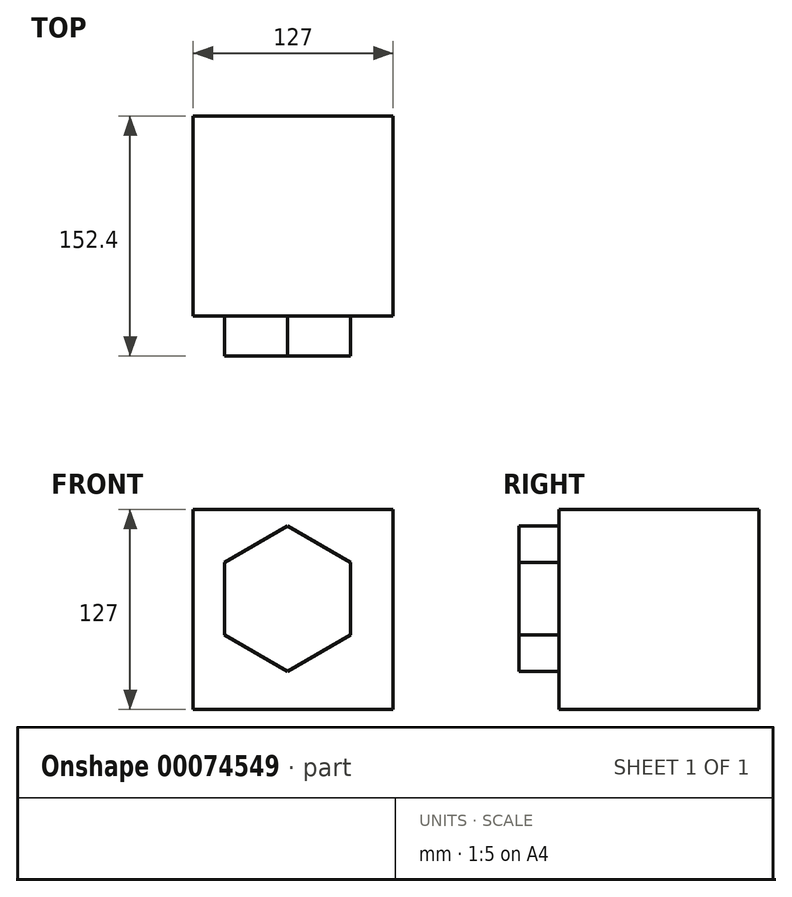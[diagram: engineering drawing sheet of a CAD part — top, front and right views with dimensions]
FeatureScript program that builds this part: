
annotation { "Feature Type Name" : "Feature", "Feature Type Description" : "" }
export const myFeature = defineFeature(function(context is Context, id is Id, definition is map)
    precondition{}
    {
        {
            var Q0;
            Q0=qCreatedBy(makeId("Front.planeOp"),FACE);
            var sketch = newSketch(context, id + "F0", { "sketchPlane" : qUnion([Q0])});
            skLineSegment(sketch, "E0.bottom", {"start": v(0, 0) * mm, "end": v(127, 0) * mm});
            skLineSegment(sketch, "E0.top", {"start": v(0, 127) * mm, "end": v(127, 127) * mm});
            skLineSegment(sketch, "E0.left", {"start": v(0, 0) * mm, "end": v(0, 127) * mm});
            skLineSegment(sketch, "E0.right", {"start": v(127, 0) * mm, "end": v(127, 127) * mm});
            skSolve(sketch);
        }
        {
            var Q0;
            Q0 = qSketchRegion(id + "F0", true);
            extrude(context, id + "F1", {"entities" : qUnion([Q0]), "depth" : 127 * mm});
        }
        {
            var Q0;
            Q0=makeQuery(id+"F1.opExtrude","CAP_FACE",FACE,{"disambiguationData":[OSD([sQuery(id+"F0.wireOp",EDGE,"E0.bottom"),sQuery(id+"F0.wireOp",EDGE,"E0.top"),sQuery(id+"F0.wireOp",EDGE,"E0.left"),sQuery(id+"F0.wireOp",EDGE,"E0.right")])],"isStart":false});
            var sketch = newSketch(context, id + "F2", { "sketchPlane" : qUnion([Q0])});
            skCircle(sketch, "E1.cCircle", {"center": v(60.04, 70.4) * mm, "radius": 46.2 * mm, "construction": true});
            skLineSegment(sketch, "E1.0", {"start": v(100.05, 47.3) * mm, "end": v(60.04, 24.2) * mm});
            skLineSegment(sketch, "E1.1", {"start": v(60.04, 24.2) * mm, "end": v(20.03, 47.3) * mm});
            skLineSegment(sketch, "E1.2", {"start": v(20.03, 47.3) * mm, "end": v(20.03, 93.5) * mm});
            skLineSegment(sketch, "E1.3", {"start": v(20.03, 93.5) * mm, "end": v(60.04, 116.6) * mm});
            skLineSegment(sketch, "E1.4", {"start": v(60.04, 116.6) * mm, "end": v(100.05, 93.5) * mm});
            skLineSegment(sketch, "E1.5", {"start": v(100.05, 93.5) * mm, "end": v(100.05, 47.3) * mm});
            skSolve(sketch);
        }
        {
            var Q0;
            Q0 = qSketchRegion(id + "F2", true);
            extrude(context, id + "F3", {"entities" : qUnion([Q0]), "operationType" : NewBodyOperationType.ADD, "depth" : 25.4 * mm});
        }
    });
